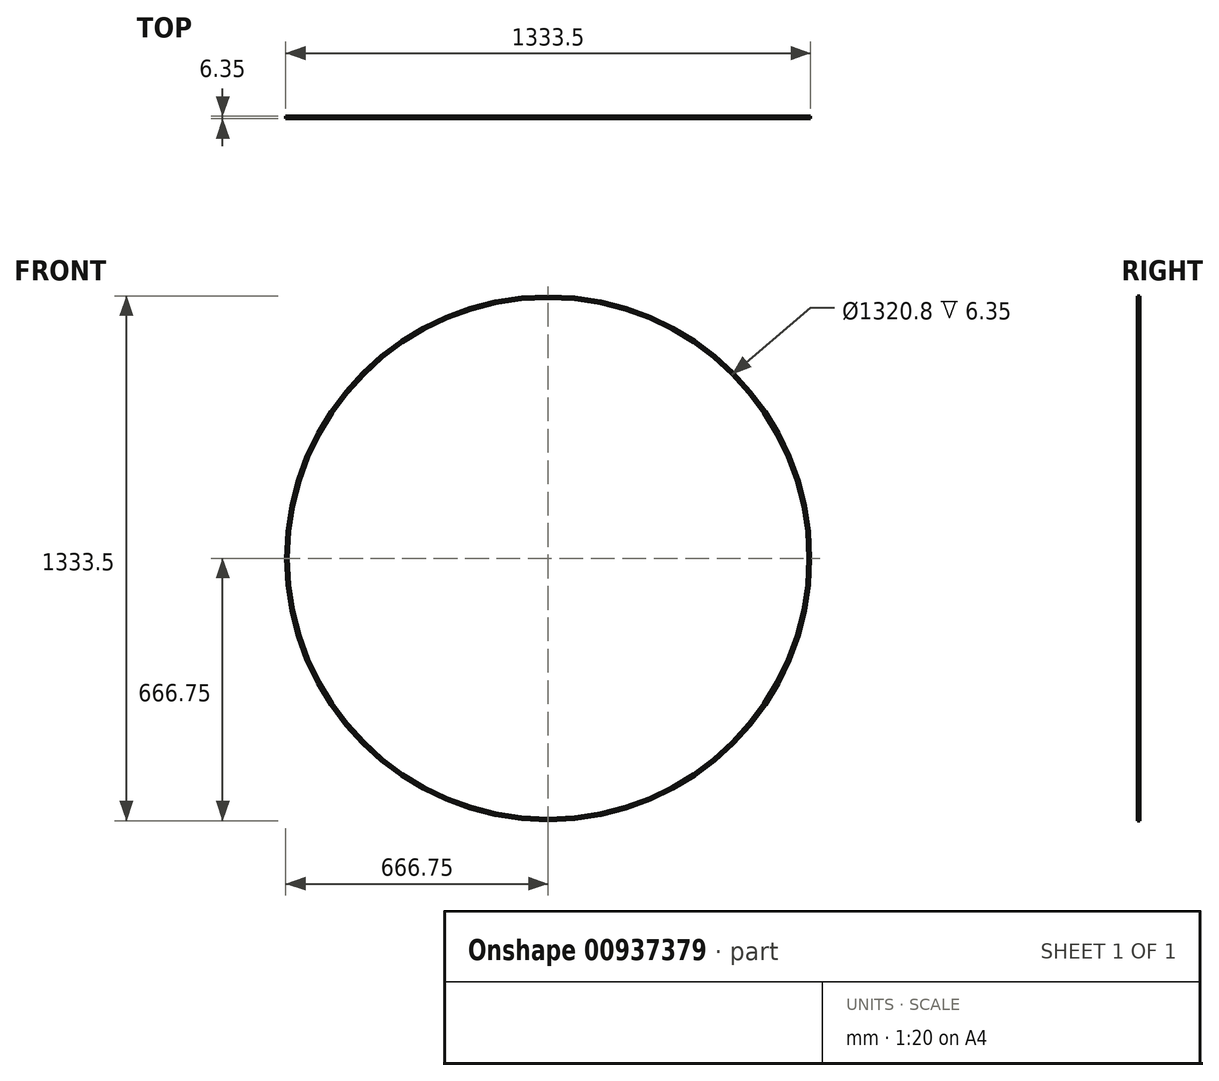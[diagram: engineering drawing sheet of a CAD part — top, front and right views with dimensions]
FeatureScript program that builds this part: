
annotation { "Feature Type Name" : "Feature", "Feature Type Description" : "" }
export const myFeature = defineFeature(function(context is Context, id is Id, definition is map)
    precondition{}
    {
        {
            var Q0;
            Q0=qCreatedBy(makeId("Front.planeOp"),FACE);
            var sketch = newSketch(context, id + "F0", { "sketchPlane" : qUnion([Q0])});
            skCircle(sketch, "E0", {"center": v(0, 0) * mm, "radius": 660.4 * mm});
            skCircle(sketch, "E1", {"center": v(0, 0) * mm, "radius": 666.75 * mm});
            skSolve(sketch);
        }
        {
            var Q0;
            Q0 = qSketchRegion(id + "F0", true);
            extrude(context, id + "F1", {"entities" : qUnion([Q0]), "depth" : 6.35 * mm, "offsetDistance" : 25.4 * mm});
        }
    });
